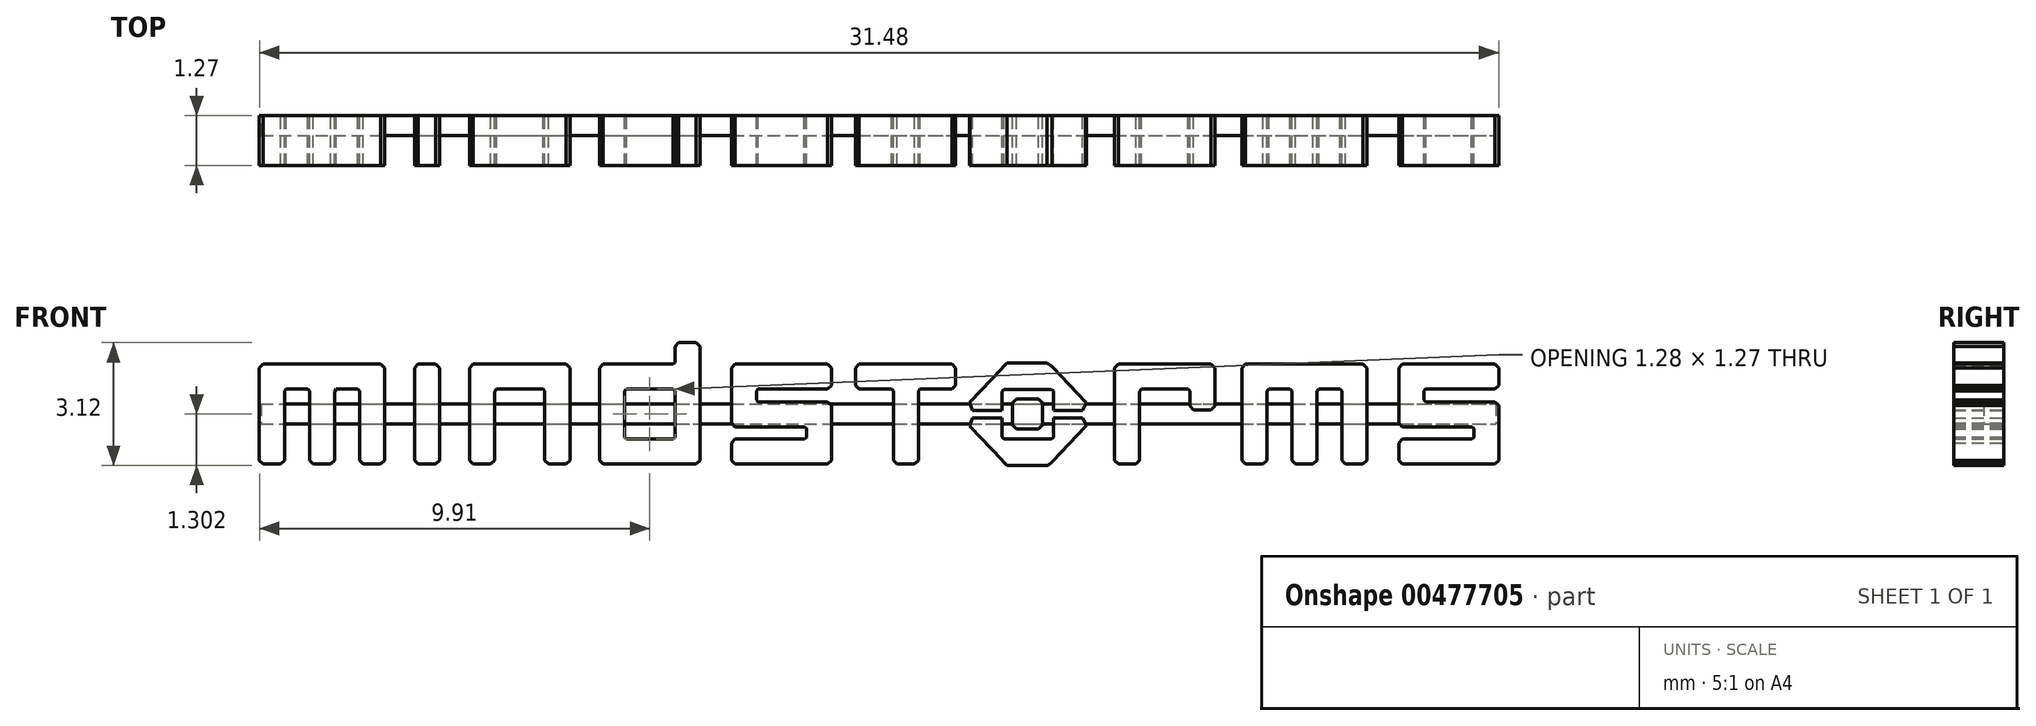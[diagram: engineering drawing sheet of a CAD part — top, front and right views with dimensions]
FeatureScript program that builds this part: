
annotation { "Feature Type Name" : "Feature", "Feature Type Description" : "" }
export const myFeature = defineFeature(function(context is Context, id is Id, definition is map)
    precondition{}
    {
        {
            var Q0;
            Q0=qCreatedBy(makeId("Front.planeOp"),FACE);
            var sketch = newSketch(context, id + "F0", { "sketchPlane" : qUnion([Q0])});
            skLineSegment(sketch, "E0", {"start": v(4.43, -0.35) * mm, "end": v(5.14, -0.35) * mm});
            skLineSegment(sketch, "E1", {"start": v(5.14, -0.35) * mm, "end": v(5.17, -0.35) * mm});
            skLineSegment(sketch, "E2", {"start": v(5.17, -0.35) * mm, "end": v(5.26, -0.55) * mm});
            skLineSegment(sketch, "E3", {"start": v(5.26, -0.55) * mm, "end": v(5.25, -0.57) * mm});
            skLineSegment(sketch, "E4", {"start": v(5.25, -0.57) * mm, "end": v(4.42, -1.44) * mm});
            skLineSegment(sketch, "E5", {"start": v(4.42, -1.44) * mm, "end": v(4.38, -1.47) * mm});
            skLineSegment(sketch, "E6", {"start": v(4.38, -1.47) * mm, "end": v(4.29, -1.56) * mm});
            skLineSegment(sketch, "E7", {"start": v(4.29, -1.56) * mm, "end": v(4.25, -1.56) * mm});
            skLineSegment(sketch, "E8", {"start": v(4.25, -1.56) * mm, "end": v(3.3, -1.56) * mm});
            skLineSegment(sketch, "E9", {"start": v(3.3, -1.56) * mm, "end": v(3.25, -1.56) * mm});
            skLineSegment(sketch, "E10", {"start": v(3.25, -1.56) * mm, "end": v(3.15, -1.46) * mm});
            skLineSegment(sketch, "E11", {"start": v(3.15, -1.46) * mm, "end": v(3.11, -1.42) * mm});
            skLineSegment(sketch, "E12", {"start": v(3.11, -1.42) * mm, "end": v(2.3, -0.57) * mm});
            skLineSegment(sketch, "E13", {"start": v(2.3, -0.57) * mm, "end": v(2.3, -0.55) * mm});
            skLineSegment(sketch, "E14", {"start": v(2.3, -0.55) * mm, "end": v(2.38, -0.35) * mm});
            skLineSegment(sketch, "E15", {"start": v(2.38, -0.35) * mm, "end": v(2.4, -0.35) * mm});
            skLineSegment(sketch, "E16", {"start": v(2.4, -0.35) * mm, "end": v(3.12, -0.35) * mm});
            skLineSegment(sketch, "E17", {"start": v(3.12, -0.35) * mm, "end": v(3.12, -0.83) * mm});
            skLineSegment(sketch, "E18", {"start": v(3.12, -0.83) * mm, "end": v(3.12, -0.84) * mm});
            skLineSegment(sketch, "E19", {"start": v(3.12, -0.84) * mm, "end": v(3.17, -0.9) * mm});
            skLineSegment(sketch, "E20", {"start": v(3.17, -0.9) * mm, "end": v(3.18, -0.9) * mm});
            skLineSegment(sketch, "E21", {"start": v(3.18, -0.9) * mm, "end": v(4.36, -0.9) * mm});
            skLineSegment(sketch, "E22", {"start": v(4.36, -0.9) * mm, "end": v(4.38, -0.9) * mm});
            skLineSegment(sketch, "E23", {"start": v(4.38, -0.9) * mm, "end": v(4.43, -0.84) * mm});
            skLineSegment(sketch, "E24", {"start": v(4.43, -0.84) * mm, "end": v(4.43, -0.83) * mm});
            skLineSegment(sketch, "E25", {"start": v(4.43, -0.83) * mm, "end": v(4.43, -0.35) * mm});
            skLineSegment(sketch, "E26", {"start": v(4.43, -0.16) * mm, "end": v(5.14, -0.16) * mm});
            skLineSegment(sketch, "E27", {"start": v(5.14, -0.16) * mm, "end": v(5.17, -0.16) * mm});
            skLineSegment(sketch, "E28", {"start": v(5.17, -0.16) * mm, "end": v(5.26, 0.04) * mm});
            skLineSegment(sketch, "E29", {"start": v(5.26, 0.04) * mm, "end": v(5.25, 0.05) * mm});
            skLineSegment(sketch, "E30", {"start": v(5.25, 0.05) * mm, "end": v(4.42, 0.93) * mm});
            skLineSegment(sketch, "E31", {"start": v(4.42, 0.93) * mm, "end": v(4.39, 0.96) * mm});
            skLineSegment(sketch, "E32", {"start": v(4.39, 0.96) * mm, "end": v(4.26, 1.05) * mm});
            skLineSegment(sketch, "E33", {"start": v(4.26, 1.05) * mm, "end": v(4.25, 1.05) * mm});
            skLineSegment(sketch, "E34", {"start": v(4.25, 1.05) * mm, "end": v(3.3, 1.05) * mm});
            skLineSegment(sketch, "E35", {"start": v(3.3, 1.05) * mm, "end": v(3.25, 1.05) * mm});
            skLineSegment(sketch, "E36", {"start": v(3.25, 1.05) * mm, "end": v(3.15, 0.94) * mm});
            skLineSegment(sketch, "E37", {"start": v(3.15, 0.94) * mm, "end": v(3.11, 0.9) * mm});
            skLineSegment(sketch, "E38", {"start": v(3.11, 0.9) * mm, "end": v(2.3, 0.05) * mm});
            skLineSegment(sketch, "E39", {"start": v(2.3, 0.05) * mm, "end": v(2.3, 0.04) * mm});
            skLineSegment(sketch, "E40", {"start": v(2.3, 0.04) * mm, "end": v(2.38, -0.16) * mm});
            skLineSegment(sketch, "E41", {"start": v(2.38, -0.16) * mm, "end": v(2.4, -0.16) * mm});
            skLineSegment(sketch, "E42", {"start": v(2.4, -0.16) * mm, "end": v(3.12, -0.16) * mm});
            skLineSegment(sketch, "E43", {"start": v(3.12, -0.16) * mm, "end": v(3.12, 0.31) * mm});
            skLineSegment(sketch, "E44", {"start": v(3.12, 0.31) * mm, "end": v(3.12, 0.32) * mm});
            skLineSegment(sketch, "E45", {"start": v(3.12, 0.32) * mm, "end": v(3.17, 0.38) * mm});
            skLineSegment(sketch, "E46", {"start": v(3.17, 0.38) * mm, "end": v(3.19, 0.38) * mm});
            skLineSegment(sketch, "E47", {"start": v(3.19, 0.38) * mm, "end": v(4.36, 0.38) * mm});
            skLineSegment(sketch, "E48", {"start": v(4.36, 0.38) * mm, "end": v(4.38, 0.38) * mm});
            skLineSegment(sketch, "E49", {"start": v(4.38, 0.38) * mm, "end": v(4.43, 0.33) * mm});
            skLineSegment(sketch, "E50", {"start": v(4.43, 0.33) * mm, "end": v(4.43, 0.31) * mm});
            skLineSegment(sketch, "E51", {"start": v(4.43, 0.31) * mm, "end": v(4.43, -0.16) * mm});
            skLineSegment(sketch, "E52", {"start": v(8.4, 1.01) * mm, "end": v(6.1, 1.01) * mm});
            skLineSegment(sketch, "E53", {"start": v(6.1, 1.01) * mm, "end": v(6.08, 1.01) * mm});
            skLineSegment(sketch, "E54", {"start": v(6.08, 1.01) * mm, "end": v(5.98, 0.92) * mm});
            skLineSegment(sketch, "E55", {"start": v(5.98, 0.92) * mm, "end": v(5.98, 0.89) * mm});
            skLineSegment(sketch, "E56", {"start": v(5.98, 0.89) * mm, "end": v(5.98, -1.4) * mm});
            skLineSegment(sketch, "E57", {"start": v(5.98, -1.4) * mm, "end": v(5.98, -1.43) * mm});
            skLineSegment(sketch, "E58", {"start": v(5.98, -1.43) * mm, "end": v(6.08, -1.53) * mm});
            skLineSegment(sketch, "E59", {"start": v(6.08, -1.53) * mm, "end": v(6.1, -1.53) * mm});
            skLineSegment(sketch, "E60", {"start": v(6.1, -1.53) * mm, "end": v(6.49, -1.53) * mm});
            skLineSegment(sketch, "E61", {"start": v(6.49, -1.53) * mm, "end": v(6.52, -1.53) * mm});
            skLineSegment(sketch, "E62", {"start": v(6.52, -1.53) * mm, "end": v(6.62, -1.43) * mm});
            skLineSegment(sketch, "E63", {"start": v(6.62, -1.43) * mm, "end": v(6.62, -1.4) * mm});
            skLineSegment(sketch, "E64", {"start": v(6.62, -1.4) * mm, "end": v(6.62, 0.32) * mm});
            skLineSegment(sketch, "E65", {"start": v(6.62, 0.32) * mm, "end": v(6.62, 0.32) * mm});
            skLineSegment(sketch, "E66", {"start": v(6.62, 0.32) * mm, "end": v(6.66, 0.38) * mm});
            skLineSegment(sketch, "E67", {"start": v(6.66, 0.38) * mm, "end": v(6.68, 0.38) * mm});
            skLineSegment(sketch, "E68", {"start": v(6.68, 0.38) * mm, "end": v(7.83, 0.38) * mm});
            skLineSegment(sketch, "E69", {"start": v(7.83, 0.38) * mm, "end": v(7.84, 0.38) * mm});
            skLineSegment(sketch, "E70", {"start": v(7.84, 0.38) * mm, "end": v(7.9, 0.33) * mm});
            skLineSegment(sketch, "E71", {"start": v(7.9, 0.33) * mm, "end": v(7.9, 0.32) * mm});
            skLineSegment(sketch, "E72", {"start": v(7.9, 0.32) * mm, "end": v(7.9, -0.02) * mm});
            skLineSegment(sketch, "E73", {"start": v(7.9, -0.02) * mm, "end": v(7.9, -0.05) * mm});
            skLineSegment(sketch, "E74", {"start": v(7.9, -0.05) * mm, "end": v(7.99, -0.15) * mm});
            skLineSegment(sketch, "E75", {"start": v(7.99, -0.15) * mm, "end": v(8.02, -0.15) * mm});
            skLineSegment(sketch, "E76", {"start": v(8.02, -0.15) * mm, "end": v(8.4, -0.15) * mm});
            skLineSegment(sketch, "E77", {"start": v(8.4, -0.15) * mm, "end": v(8.43, -0.15) * mm});
            skLineSegment(sketch, "E78", {"start": v(8.43, -0.15) * mm, "end": v(8.53, -0.05) * mm});
            skLineSegment(sketch, "E79", {"start": v(8.53, -0.05) * mm, "end": v(8.53, -0.02) * mm});
            skLineSegment(sketch, "E80", {"start": v(8.53, -0.02) * mm, "end": v(8.53, 0.89) * mm});
            skLineSegment(sketch, "E81", {"start": v(8.53, 0.89) * mm, "end": v(8.53, 0.92) * mm});
            skLineSegment(sketch, "E82", {"start": v(8.53, 0.92) * mm, "end": v(8.43, 1.01) * mm});
            skLineSegment(sketch, "E83", {"start": v(8.43, 1.01) * mm, "end": v(8.4, 1.01) * mm});
            skLineSegment(sketch, "E84", {"start": v(13.84, 0.32) * mm, "end": v(13.84, 0.33) * mm});
            skLineSegment(sketch, "E85", {"start": v(13.84, 0.33) * mm, "end": v(13.88, 0.38) * mm});
            skLineSegment(sketch, "E86", {"start": v(13.88, 0.38) * mm, "end": v(13.9, 0.38) * mm});
            skLineSegment(sketch, "E87", {"start": v(13.9, 0.38) * mm, "end": v(15.62, 0.38) * mm});
            skLineSegment(sketch, "E88", {"start": v(15.62, 0.38) * mm, "end": v(15.65, 0.38) * mm});
            skLineSegment(sketch, "E89", {"start": v(15.65, 0.38) * mm, "end": v(15.74, 0.47) * mm});
            skLineSegment(sketch, "E90", {"start": v(15.74, 0.47) * mm, "end": v(15.74, 0.5) * mm});
            skLineSegment(sketch, "E91", {"start": v(15.74, 0.5) * mm, "end": v(15.74, 0.89) * mm});
            skLineSegment(sketch, "E92", {"start": v(15.74, 0.89) * mm, "end": v(15.74, 0.92) * mm});
            skLineSegment(sketch, "E93", {"start": v(15.74, 0.92) * mm, "end": v(15.65, 1.01) * mm});
            skLineSegment(sketch, "E94", {"start": v(15.65, 1.01) * mm, "end": v(15.62, 1.01) * mm});
            skLineSegment(sketch, "E95", {"start": v(15.62, 1.01) * mm, "end": v(13.33, 1.01) * mm});
            skLineSegment(sketch, "E96", {"start": v(13.33, 1.01) * mm, "end": v(13.3, 1.01) * mm});
            skLineSegment(sketch, "E97", {"start": v(13.3, 1.01) * mm, "end": v(13.2, 0.92) * mm});
            skLineSegment(sketch, "E98", {"start": v(13.2, 0.92) * mm, "end": v(13.2, 0.89) * mm});
            skLineSegment(sketch, "E99", {"start": v(13.2, 0.89) * mm, "end": v(13.2, -0.45) * mm});
            skLineSegment(sketch, "E100", {"start": v(13.2, -0.45) * mm, "end": v(13.2, -0.48) * mm});
            skLineSegment(sketch, "E101", {"start": v(13.2, -0.48) * mm, "end": v(13.3, -0.58) * mm});
            skLineSegment(sketch, "E102", {"start": v(13.3, -0.58) * mm, "end": v(13.33, -0.58) * mm});
            skLineSegment(sketch, "E103", {"start": v(13.33, -0.58) * mm, "end": v(15.05, -0.58) * mm});
            skLineSegment(sketch, "E104", {"start": v(15.05, -0.58) * mm, "end": v(15.06, -0.58) * mm});
            skLineSegment(sketch, "E105", {"start": v(15.06, -0.58) * mm, "end": v(15.1, -0.62) * mm});
            skLineSegment(sketch, "E106", {"start": v(15.1, -0.62) * mm, "end": v(15.1, -0.64) * mm});
            skLineSegment(sketch, "E107", {"start": v(15.1, -0.64) * mm, "end": v(15.1, -0.83) * mm});
            skLineSegment(sketch, "E108", {"start": v(15.1, -0.83) * mm, "end": v(15.1, -0.85) * mm});
            skLineSegment(sketch, "E109", {"start": v(15.1, -0.85) * mm, "end": v(15.06, -0.9) * mm});
            skLineSegment(sketch, "E110", {"start": v(15.06, -0.9) * mm, "end": v(15.05, -0.9) * mm});
            skLineSegment(sketch, "E111", {"start": v(15.05, -0.9) * mm, "end": v(13.33, -0.9) * mm});
            skLineSegment(sketch, "E112", {"start": v(13.33, -0.9) * mm, "end": v(13.3, -0.9) * mm});
            skLineSegment(sketch, "E113", {"start": v(13.3, -0.9) * mm, "end": v(13.2, -1) * mm});
            skLineSegment(sketch, "E114", {"start": v(13.2, -1) * mm, "end": v(13.2, -1.02) * mm});
            skLineSegment(sketch, "E115", {"start": v(13.2, -1.02) * mm, "end": v(13.2, -1.4) * mm});
            skLineSegment(sketch, "E116", {"start": v(13.2, -1.4) * mm, "end": v(13.2, -1.43) * mm});
            skLineSegment(sketch, "E117", {"start": v(13.2, -1.43) * mm, "end": v(13.3, -1.53) * mm});
            skLineSegment(sketch, "E118", {"start": v(13.3, -1.53) * mm, "end": v(13.33, -1.53) * mm});
            skLineSegment(sketch, "E119", {"start": v(13.33, -1.53) * mm, "end": v(15.62, -1.53) * mm});
            skLineSegment(sketch, "E120", {"start": v(15.62, -1.53) * mm, "end": v(15.65, -1.53) * mm});
            skLineSegment(sketch, "E121", {"start": v(15.65, -1.53) * mm, "end": v(15.74, -1.43) * mm});
            skLineSegment(sketch, "E122", {"start": v(15.74, -1.43) * mm, "end": v(15.74, -1.4) * mm});
            skLineSegment(sketch, "E123", {"start": v(15.74, -1.4) * mm, "end": v(15.74, -0.07) * mm});
            skLineSegment(sketch, "E124", {"start": v(15.74, -0.07) * mm, "end": v(15.74, -0.04) * mm});
            skLineSegment(sketch, "E125", {"start": v(15.74, -0.04) * mm, "end": v(15.65, 0.06) * mm});
            skLineSegment(sketch, "E126", {"start": v(15.65, 0.06) * mm, "end": v(15.62, 0.06) * mm});
            skLineSegment(sketch, "E127", {"start": v(15.62, 0.06) * mm, "end": v(13.9, 0.06) * mm});
            skLineSegment(sketch, "E128", {"start": v(13.9, 0.06) * mm, "end": v(13.88, 0.06) * mm});
            skLineSegment(sketch, "E129", {"start": v(13.88, 0.06) * mm, "end": v(13.84, 0.1) * mm});
            skLineSegment(sketch, "E130", {"start": v(13.84, 0.1) * mm, "end": v(13.84, 0.12) * mm});
            skLineSegment(sketch, "E131", {"start": v(13.84, 0.12) * mm, "end": v(13.84, 0.32) * mm});
            skLineSegment(sketch, "E132", {"start": v(-3.12, 0.32) * mm, "end": v(-3.12, 0.33) * mm});
            skLineSegment(sketch, "E133", {"start": v(-3.12, 0.33) * mm, "end": v(-3.08, 0.38) * mm});
            skLineSegment(sketch, "E134", {"start": v(-3.08, 0.38) * mm, "end": v(-3.06, 0.38) * mm});
            skLineSegment(sketch, "E135", {"start": v(-3.06, 0.38) * mm, "end": v(-1.34, 0.38) * mm});
            skLineSegment(sketch, "E136", {"start": v(-1.34, 0.38) * mm, "end": v(-1.31, 0.38) * mm});
            skLineSegment(sketch, "E137", {"start": v(-1.31, 0.38) * mm, "end": v(-1.21, 0.47) * mm});
            skLineSegment(sketch, "E138", {"start": v(-1.21, 0.47) * mm, "end": v(-1.21, 0.5) * mm});
            skLineSegment(sketch, "E139", {"start": v(-1.21, 0.5) * mm, "end": v(-1.21, 0.89) * mm});
            skLineSegment(sketch, "E140", {"start": v(-1.21, 0.89) * mm, "end": v(-1.21, 0.92) * mm});
            skLineSegment(sketch, "E141", {"start": v(-1.21, 0.92) * mm, "end": v(-1.31, 1.01) * mm});
            skLineSegment(sketch, "E142", {"start": v(-1.31, 1.01) * mm, "end": v(-1.34, 1.01) * mm});
            skLineSegment(sketch, "E143", {"start": v(-1.34, 1.01) * mm, "end": v(-3.63, 1.01) * mm});
            skLineSegment(sketch, "E144", {"start": v(-3.63, 1.01) * mm, "end": v(-3.66, 1.01) * mm});
            skLineSegment(sketch, "E145", {"start": v(-3.66, 1.01) * mm, "end": v(-3.76, 0.92) * mm});
            skLineSegment(sketch, "E146", {"start": v(-3.76, 0.92) * mm, "end": v(-3.76, 0.89) * mm});
            skLineSegment(sketch, "E147", {"start": v(-3.76, 0.89) * mm, "end": v(-3.76, -0.45) * mm});
            skLineSegment(sketch, "E148", {"start": v(-3.76, -0.45) * mm, "end": v(-3.76, -0.48) * mm});
            skLineSegment(sketch, "E149", {"start": v(-3.76, -0.48) * mm, "end": v(-3.66, -0.58) * mm});
            skLineSegment(sketch, "E150", {"start": v(-3.66, -0.58) * mm, "end": v(-3.63, -0.58) * mm});
            skLineSegment(sketch, "E151", {"start": v(-3.63, -0.58) * mm, "end": v(-1.9, -0.58) * mm});
            skLineSegment(sketch, "E152", {"start": v(-1.9, -0.58) * mm, "end": v(-1.9, -0.58) * mm});
            skLineSegment(sketch, "E153", {"start": v(-1.9, -0.58) * mm, "end": v(-1.85, -0.62) * mm});
            skLineSegment(sketch, "E154", {"start": v(-1.85, -0.62) * mm, "end": v(-1.85, -0.64) * mm});
            skLineSegment(sketch, "E155", {"start": v(-1.85, -0.64) * mm, "end": v(-1.85, -0.83) * mm});
            skLineSegment(sketch, "E156", {"start": v(-1.85, -0.83) * mm, "end": v(-1.85, -0.85) * mm});
            skLineSegment(sketch, "E157", {"start": v(-1.85, -0.85) * mm, "end": v(-1.9, -0.9) * mm});
            skLineSegment(sketch, "E158", {"start": v(-1.9, -0.9) * mm, "end": v(-1.9, -0.9) * mm});
            skLineSegment(sketch, "E159", {"start": v(-1.9, -0.9) * mm, "end": v(-3.63, -0.9) * mm});
            skLineSegment(sketch, "E160", {"start": v(-3.63, -0.9) * mm, "end": v(-3.66, -0.9) * mm});
            skLineSegment(sketch, "E161", {"start": v(-3.66, -0.9) * mm, "end": v(-3.76, -1) * mm});
            skLineSegment(sketch, "E162", {"start": v(-3.76, -1) * mm, "end": v(-3.76, -1.02) * mm});
            skLineSegment(sketch, "E163", {"start": v(-3.76, -1.02) * mm, "end": v(-3.76, -1.4) * mm});
            skLineSegment(sketch, "E164", {"start": v(-3.76, -1.4) * mm, "end": v(-3.76, -1.43) * mm});
            skLineSegment(sketch, "E165", {"start": v(-3.76, -1.43) * mm, "end": v(-3.66, -1.53) * mm});
            skLineSegment(sketch, "E166", {"start": v(-3.66, -1.53) * mm, "end": v(-3.63, -1.53) * mm});
            skLineSegment(sketch, "E167", {"start": v(-3.63, -1.53) * mm, "end": v(-1.34, -1.53) * mm});
            skLineSegment(sketch, "E168", {"start": v(-1.34, -1.53) * mm, "end": v(-1.31, -1.53) * mm});
            skLineSegment(sketch, "E169", {"start": v(-1.31, -1.53) * mm, "end": v(-1.21, -1.43) * mm});
            skLineSegment(sketch, "E170", {"start": v(-1.21, -1.43) * mm, "end": v(-1.21, -1.4) * mm});
            skLineSegment(sketch, "E171", {"start": v(-1.21, -1.4) * mm, "end": v(-1.21, -0.07) * mm});
            skLineSegment(sketch, "E172", {"start": v(-1.21, -0.07) * mm, "end": v(-1.21, -0.04) * mm});
            skLineSegment(sketch, "E173", {"start": v(-1.21, -0.04) * mm, "end": v(-1.31, 0.06) * mm});
            skLineSegment(sketch, "E174", {"start": v(-1.31, 0.06) * mm, "end": v(-1.34, 0.06) * mm});
            skLineSegment(sketch, "E175", {"start": v(-1.34, 0.06) * mm, "end": v(-3.06, 0.06) * mm});
            skLineSegment(sketch, "E176", {"start": v(-3.06, 0.06) * mm, "end": v(-3.07, 0.06) * mm});
            skLineSegment(sketch, "E177", {"start": v(-3.07, 0.06) * mm, "end": v(-3.12, 0.1) * mm});
            skLineSegment(sketch, "E178", {"start": v(-3.12, 0.1) * mm, "end": v(-3.12, 0.12) * mm});
            skLineSegment(sketch, "E179", {"start": v(-3.12, 0.12) * mm, "end": v(-3.12, 0.32) * mm});
            skLineSegment(sketch, "E180", {"start": v(-5.2, -0.83) * mm, "end": v(-5.2, -0.85) * mm});
            skLineSegment(sketch, "E181", {"start": v(-5.2, -0.85) * mm, "end": v(-5.24, -0.9) * mm});
            skLineSegment(sketch, "E182", {"start": v(-5.24, -0.9) * mm, "end": v(-5.25, -0.9) * mm});
            skLineSegment(sketch, "E183", {"start": v(-5.25, -0.9) * mm, "end": v(-6.4, -0.9) * mm});
            skLineSegment(sketch, "E184", {"start": v(-6.4, -0.9) * mm, "end": v(-6.42, -0.9) * mm});
            skLineSegment(sketch, "E185", {"start": v(-6.42, -0.9) * mm, "end": v(-6.47, -0.85) * mm});
            skLineSegment(sketch, "E186", {"start": v(-6.47, -0.85) * mm, "end": v(-6.47, -0.83) * mm});
            skLineSegment(sketch, "E187", {"start": v(-6.47, -0.83) * mm, "end": v(-6.47, 0.32) * mm});
            skLineSegment(sketch, "E188", {"start": v(-6.47, 0.32) * mm, "end": v(-6.47, 0.33) * mm});
            skLineSegment(sketch, "E189", {"start": v(-6.47, 0.33) * mm, "end": v(-6.42, 0.38) * mm});
            skLineSegment(sketch, "E190", {"start": v(-6.42, 0.38) * mm, "end": v(-6.4, 0.38) * mm});
            skLineSegment(sketch, "E191", {"start": v(-6.4, 0.38) * mm, "end": v(-5.25, 0.38) * mm});
            skLineSegment(sketch, "E192", {"start": v(-5.25, 0.38) * mm, "end": v(-5.24, 0.38) * mm});
            skLineSegment(sketch, "E193", {"start": v(-5.24, 0.38) * mm, "end": v(-5.2, 0.33) * mm});
            skLineSegment(sketch, "E194", {"start": v(-5.2, 0.33) * mm, "end": v(-5.2, 0.32) * mm});
            skLineSegment(sketch, "E195", {"start": v(-5.2, 0.32) * mm, "end": v(-5.2, -0.83) * mm});
            skLineSegment(sketch, "E196", {"start": v(-4.68, 1.56) * mm, "end": v(-5.06, 1.56) * mm});
            skLineSegment(sketch, "E197", {"start": v(-5.06, 1.56) * mm, "end": v(-5.1, 1.56) * mm});
            skLineSegment(sketch, "E198", {"start": v(-5.1, 1.56) * mm, "end": v(-5.2, 1.47) * mm});
            skLineSegment(sketch, "E199", {"start": v(-5.2, 1.47) * mm, "end": v(-5.2, 1.43) * mm});
            skLineSegment(sketch, "E200", {"start": v(-5.2, 1.43) * mm, "end": v(-5.2, 1.08) * mm});
            skLineSegment(sketch, "E201", {"start": v(-5.2, 1.08) * mm, "end": v(-5.2, 1.06) * mm});
            skLineSegment(sketch, "E202", {"start": v(-5.2, 1.06) * mm, "end": v(-5.24, 1.01) * mm});
            skLineSegment(sketch, "E203", {"start": v(-5.24, 1.01) * mm, "end": v(-5.25, 1.01) * mm});
            skLineSegment(sketch, "E204", {"start": v(-5.25, 1.01) * mm, "end": v(-6.98, 1.01) * mm});
            skLineSegment(sketch, "E205", {"start": v(-6.98, 1.01) * mm, "end": v(-7.01, 1.01) * mm});
            skLineSegment(sketch, "E206", {"start": v(-7.01, 1.01) * mm, "end": v(-7.1, 0.92) * mm});
            skLineSegment(sketch, "E207", {"start": v(-7.1, 0.92) * mm, "end": v(-7.1, 0.89) * mm});
            skLineSegment(sketch, "E208", {"start": v(-7.1, 0.89) * mm, "end": v(-7.1, -1.4) * mm});
            skLineSegment(sketch, "E209", {"start": v(-7.1, -1.4) * mm, "end": v(-7.1, -1.43) * mm});
            skLineSegment(sketch, "E210", {"start": v(-7.1, -1.43) * mm, "end": v(-7.01, -1.53) * mm});
            skLineSegment(sketch, "E211", {"start": v(-7.01, -1.53) * mm, "end": v(-6.98, -1.53) * mm});
            skLineSegment(sketch, "E212", {"start": v(-6.98, -1.53) * mm, "end": v(-4.68, -1.53) * mm});
            skLineSegment(sketch, "E213", {"start": v(-4.68, -1.53) * mm, "end": v(-4.65, -1.53) * mm});
            skLineSegment(sketch, "E214", {"start": v(-4.65, -1.53) * mm, "end": v(-4.56, -1.43) * mm});
            skLineSegment(sketch, "E215", {"start": v(-4.56, -1.43) * mm, "end": v(-4.56, -1.4) * mm});
            skLineSegment(sketch, "E216", {"start": v(-4.56, -1.4) * mm, "end": v(-4.56, 1.43) * mm});
            skLineSegment(sketch, "E217", {"start": v(-4.56, 1.43) * mm, "end": v(-4.56, 1.47) * mm});
            skLineSegment(sketch, "E218", {"start": v(-4.56, 1.47) * mm, "end": v(-4.65, 1.56) * mm});
            skLineSegment(sketch, "E219", {"start": v(-4.65, 1.56) * mm, "end": v(-4.68, 1.56) * mm});
            skLineSegment(sketch, "E220", {"start": v(1.81, 1.01) * mm, "end": v(-0.47, 1.01) * mm});
            skLineSegment(sketch, "E221", {"start": v(-0.47, 1.01) * mm, "end": v(-0.5, 1.01) * mm});
            skLineSegment(sketch, "E222", {"start": v(-0.5, 1.01) * mm, "end": v(-0.6, 0.92) * mm});
            skLineSegment(sketch, "E223", {"start": v(-0.6, 0.92) * mm, "end": v(-0.6, 0.89) * mm});
            skLineSegment(sketch, "E224", {"start": v(-0.6, 0.89) * mm, "end": v(-0.6, 0.5) * mm});
            skLineSegment(sketch, "E225", {"start": v(-0.6, 0.5) * mm, "end": v(-0.6, 0.47) * mm});
            skLineSegment(sketch, "E226", {"start": v(-0.6, 0.47) * mm, "end": v(-0.5, 0.38) * mm});
            skLineSegment(sketch, "E227", {"start": v(-0.5, 0.38) * mm, "end": v(-0.47, 0.38) * mm});
            skLineSegment(sketch, "E228", {"start": v(-0.47, 0.38) * mm, "end": v(0.3, 0.38) * mm});
            skLineSegment(sketch, "E229", {"start": v(0.3, 0.38) * mm, "end": v(0.31, 0.38) * mm});
            skLineSegment(sketch, "E230", {"start": v(0.31, 0.38) * mm, "end": v(0.36, 0.33) * mm});
            skLineSegment(sketch, "E231", {"start": v(0.36, 0.33) * mm, "end": v(0.36, 0.32) * mm});
            skLineSegment(sketch, "E232", {"start": v(0.36, 0.32) * mm, "end": v(0.36, -1.4) * mm});
            skLineSegment(sketch, "E233", {"start": v(0.36, -1.4) * mm, "end": v(0.36, -1.43) * mm});
            skLineSegment(sketch, "E234", {"start": v(0.36, -1.43) * mm, "end": v(0.45, -1.53) * mm});
            skLineSegment(sketch, "E235", {"start": v(0.45, -1.53) * mm, "end": v(0.49, -1.53) * mm});
            skLineSegment(sketch, "E236", {"start": v(0.49, -1.53) * mm, "end": v(0.87, -1.53) * mm});
            skLineSegment(sketch, "E237", {"start": v(0.87, -1.53) * mm, "end": v(0.9, -1.53) * mm});
            skLineSegment(sketch, "E238", {"start": v(0.9, -1.53) * mm, "end": v(1, -1.43) * mm});
            skLineSegment(sketch, "E239", {"start": v(1, -1.43) * mm, "end": v(1, -1.4) * mm});
            skLineSegment(sketch, "E240", {"start": v(1, -1.4) * mm, "end": v(1, 0.32) * mm});
            skLineSegment(sketch, "E241", {"start": v(1, 0.32) * mm, "end": v(1, 0.33) * mm});
            skLineSegment(sketch, "E242", {"start": v(1, 0.33) * mm, "end": v(1.04, 0.38) * mm});
            skLineSegment(sketch, "E243", {"start": v(1.04, 0.38) * mm, "end": v(1.06, 0.38) * mm});
            skLineSegment(sketch, "E244", {"start": v(1.06, 0.38) * mm, "end": v(1.81, 0.38) * mm});
            skLineSegment(sketch, "E245", {"start": v(1.81, 0.38) * mm, "end": v(1.84, 0.38) * mm});
            skLineSegment(sketch, "E246", {"start": v(1.84, 0.38) * mm, "end": v(1.94, 0.47) * mm});
            skLineSegment(sketch, "E247", {"start": v(1.94, 0.47) * mm, "end": v(1.94, 0.5) * mm});
            skLineSegment(sketch, "E248", {"start": v(1.94, 0.5) * mm, "end": v(1.94, 0.89) * mm});
            skLineSegment(sketch, "E249", {"start": v(1.94, 0.89) * mm, "end": v(1.94, 0.92) * mm});
            skLineSegment(sketch, "E250", {"start": v(1.94, 0.92) * mm, "end": v(1.84, 1.01) * mm});
            skLineSegment(sketch, "E251", {"start": v(1.84, 1.01) * mm, "end": v(1.81, 1.01) * mm});
            skLineSegment(sketch, "E252", {"start": v(-7.98, 1.01) * mm, "end": v(-10.28, 1.01) * mm});
            skLineSegment(sketch, "E253", {"start": v(-10.28, 1.01) * mm, "end": v(-10.31, 1.01) * mm});
            skLineSegment(sketch, "E254", {"start": v(-10.31, 1.01) * mm, "end": v(-10.4, 0.92) * mm});
            skLineSegment(sketch, "E255", {"start": v(-10.4, 0.92) * mm, "end": v(-10.4, 0.89) * mm});
            skLineSegment(sketch, "E256", {"start": v(-10.4, 0.89) * mm, "end": v(-10.4, -1.4) * mm});
            skLineSegment(sketch, "E257", {"start": v(-10.4, -1.4) * mm, "end": v(-10.4, -1.43) * mm});
            skLineSegment(sketch, "E258", {"start": v(-10.4, -1.43) * mm, "end": v(-10.31, -1.53) * mm});
            skLineSegment(sketch, "E259", {"start": v(-10.31, -1.53) * mm, "end": v(-10.28, -1.53) * mm});
            skLineSegment(sketch, "E260", {"start": v(-10.28, -1.53) * mm, "end": v(-9.9, -1.53) * mm});
            skLineSegment(sketch, "E261", {"start": v(-9.9, -1.53) * mm, "end": v(-9.87, -1.53) * mm});
            skLineSegment(sketch, "E262", {"start": v(-9.87, -1.53) * mm, "end": v(-9.77, -1.43) * mm});
            skLineSegment(sketch, "E263", {"start": v(-9.77, -1.43) * mm, "end": v(-9.77, -1.4) * mm});
            skLineSegment(sketch, "E264", {"start": v(-9.77, -1.4) * mm, "end": v(-9.77, 0.32) * mm});
            skLineSegment(sketch, "E265", {"start": v(-9.77, 0.32) * mm, "end": v(-9.77, 0.32) * mm});
            skLineSegment(sketch, "E266", {"start": v(-9.77, 0.32) * mm, "end": v(-9.72, 0.38) * mm});
            skLineSegment(sketch, "E267", {"start": v(-9.72, 0.38) * mm, "end": v(-9.7, 0.38) * mm});
            skLineSegment(sketch, "E268", {"start": v(-9.7, 0.38) * mm, "end": v(-8.56, 0.38) * mm});
            skLineSegment(sketch, "E269", {"start": v(-8.56, 0.38) * mm, "end": v(-8.54, 0.38) * mm});
            skLineSegment(sketch, "E270", {"start": v(-8.54, 0.38) * mm, "end": v(-8.5, 0.33) * mm});
            skLineSegment(sketch, "E271", {"start": v(-8.5, 0.33) * mm, "end": v(-8.5, 0.32) * mm});
            skLineSegment(sketch, "E272", {"start": v(-8.5, 0.32) * mm, "end": v(-8.5, -1.4) * mm});
            skLineSegment(sketch, "E273", {"start": v(-8.5, -1.4) * mm, "end": v(-8.5, -1.43) * mm});
            skLineSegment(sketch, "E274", {"start": v(-8.5, -1.43) * mm, "end": v(-8.4, -1.53) * mm});
            skLineSegment(sketch, "E275", {"start": v(-8.4, -1.53) * mm, "end": v(-8.37, -1.53) * mm});
            skLineSegment(sketch, "E276", {"start": v(-8.37, -1.53) * mm, "end": v(-7.98, -1.53) * mm});
            skLineSegment(sketch, "E277", {"start": v(-7.98, -1.53) * mm, "end": v(-7.95, -1.53) * mm});
            skLineSegment(sketch, "E278", {"start": v(-7.95, -1.53) * mm, "end": v(-7.86, -1.43) * mm});
            skLineSegment(sketch, "E279", {"start": v(-7.86, -1.43) * mm, "end": v(-7.86, -1.4) * mm});
            skLineSegment(sketch, "E280", {"start": v(-7.86, -1.4) * mm, "end": v(-7.86, 0.89) * mm});
            skLineSegment(sketch, "E281", {"start": v(-7.86, 0.89) * mm, "end": v(-7.86, 0.92) * mm});
            skLineSegment(sketch, "E282", {"start": v(-7.86, 0.92) * mm, "end": v(-7.95, 1.01) * mm});
            skLineSegment(sketch, "E283", {"start": v(-7.95, 1.01) * mm, "end": v(-7.98, 1.01) * mm});
            skLineSegment(sketch, "E284", {"start": v(12.26, 1.01) * mm, "end": v(9.34, 1.01) * mm});
            skLineSegment(sketch, "E285", {"start": v(9.34, 1.01) * mm, "end": v(9.31, 1.01) * mm});
            skLineSegment(sketch, "E286", {"start": v(9.31, 1.01) * mm, "end": v(9.21, 0.92) * mm});
            skLineSegment(sketch, "E287", {"start": v(9.21, 0.92) * mm, "end": v(9.21, 0.89) * mm});
            skLineSegment(sketch, "E288", {"start": v(9.21, 0.89) * mm, "end": v(9.21, -1.4) * mm});
            skLineSegment(sketch, "E289", {"start": v(9.21, -1.4) * mm, "end": v(9.21, -1.43) * mm});
            skLineSegment(sketch, "E290", {"start": v(9.21, -1.43) * mm, "end": v(9.31, -1.53) * mm});
            skLineSegment(sketch, "E291", {"start": v(9.31, -1.53) * mm, "end": v(9.34, -1.53) * mm});
            skLineSegment(sketch, "E292", {"start": v(9.34, -1.53) * mm, "end": v(9.72, -1.53) * mm});
            skLineSegment(sketch, "E293", {"start": v(9.72, -1.53) * mm, "end": v(9.75, -1.53) * mm});
            skLineSegment(sketch, "E294", {"start": v(9.75, -1.53) * mm, "end": v(9.85, -1.43) * mm});
            skLineSegment(sketch, "E295", {"start": v(9.85, -1.43) * mm, "end": v(9.85, -1.4) * mm});
            skLineSegment(sketch, "E296", {"start": v(9.85, -1.4) * mm, "end": v(9.85, 0.32) * mm});
            skLineSegment(sketch, "E297", {"start": v(9.85, 0.32) * mm, "end": v(9.85, 0.33) * mm});
            skLineSegment(sketch, "E298", {"start": v(9.85, 0.33) * mm, "end": v(9.9, 0.38) * mm});
            skLineSegment(sketch, "E299", {"start": v(9.9, 0.38) * mm, "end": v(9.91, 0.38) * mm});
            skLineSegment(sketch, "E300", {"start": v(9.91, 0.38) * mm, "end": v(10.42, 0.38) * mm});
            skLineSegment(sketch, "E301", {"start": v(10.42, 0.38) * mm, "end": v(10.44, 0.38) * mm});
            skLineSegment(sketch, "E302", {"start": v(10.44, 0.38) * mm, "end": v(10.48, 0.33) * mm});
            skLineSegment(sketch, "E303", {"start": v(10.48, 0.33) * mm, "end": v(10.48, 0.32) * mm});
            skLineSegment(sketch, "E304", {"start": v(10.48, 0.32) * mm, "end": v(10.48, -1.4) * mm});
            skLineSegment(sketch, "E305", {"start": v(10.48, -1.4) * mm, "end": v(10.48, -1.43) * mm});
            skLineSegment(sketch, "E306", {"start": v(10.48, -1.43) * mm, "end": v(10.58, -1.53) * mm});
            skLineSegment(sketch, "E307", {"start": v(10.58, -1.53) * mm, "end": v(10.61, -1.53) * mm});
            skLineSegment(sketch, "E308", {"start": v(10.61, -1.53) * mm, "end": v(11, -1.53) * mm});
            skLineSegment(sketch, "E309", {"start": v(11, -1.53) * mm, "end": v(11.02, -1.53) * mm});
            skLineSegment(sketch, "E310", {"start": v(11.02, -1.53) * mm, "end": v(11.12, -1.43) * mm});
            skLineSegment(sketch, "E311", {"start": v(11.12, -1.43) * mm, "end": v(11.12, -1.4) * mm});
            skLineSegment(sketch, "E312", {"start": v(11.12, -1.4) * mm, "end": v(11.12, 0.32) * mm});
            skLineSegment(sketch, "E313", {"start": v(11.12, 0.32) * mm, "end": v(11.12, 0.33) * mm});
            skLineSegment(sketch, "E314", {"start": v(11.12, 0.33) * mm, "end": v(11.17, 0.38) * mm});
            skLineSegment(sketch, "E315", {"start": v(11.17, 0.38) * mm, "end": v(11.18, 0.38) * mm});
            skLineSegment(sketch, "E316", {"start": v(11.18, 0.38) * mm, "end": v(11.7, 0.38) * mm});
            skLineSegment(sketch, "E317", {"start": v(11.7, 0.38) * mm, "end": v(11.7, 0.38) * mm});
            skLineSegment(sketch, "E318", {"start": v(11.7, 0.38) * mm, "end": v(11.76, 0.33) * mm});
            skLineSegment(sketch, "E319", {"start": v(11.76, 0.33) * mm, "end": v(11.76, 0.32) * mm});
            skLineSegment(sketch, "E320", {"start": v(11.76, 0.32) * mm, "end": v(11.76, -1.4) * mm});
            skLineSegment(sketch, "E321", {"start": v(11.76, -1.4) * mm, "end": v(11.76, -1.43) * mm});
            skLineSegment(sketch, "E322", {"start": v(11.76, -1.43) * mm, "end": v(11.85, -1.53) * mm});
            skLineSegment(sketch, "E323", {"start": v(11.85, -1.53) * mm, "end": v(11.88, -1.53) * mm});
            skLineSegment(sketch, "E324", {"start": v(11.88, -1.53) * mm, "end": v(12.26, -1.53) * mm});
            skLineSegment(sketch, "E325", {"start": v(12.26, -1.53) * mm, "end": v(12.3, -1.53) * mm});
            skLineSegment(sketch, "E326", {"start": v(12.3, -1.53) * mm, "end": v(12.4, -1.43) * mm});
            skLineSegment(sketch, "E327", {"start": v(12.4, -1.43) * mm, "end": v(12.4, -1.4) * mm});
            skLineSegment(sketch, "E328", {"start": v(12.4, -1.4) * mm, "end": v(12.4, 0.89) * mm});
            skLineSegment(sketch, "E329", {"start": v(12.4, 0.89) * mm, "end": v(12.4, 0.92) * mm});
            skLineSegment(sketch, "E330", {"start": v(12.4, 0.92) * mm, "end": v(12.3, 1.01) * mm});
            skLineSegment(sketch, "E331", {"start": v(12.3, 1.01) * mm, "end": v(12.26, 1.01) * mm});
            skLineSegment(sketch, "E332", {"start": v(-12.7, 1.01) * mm, "end": v(-15.62, 1.01) * mm});
            skLineSegment(sketch, "E333", {"start": v(-15.62, 1.01) * mm, "end": v(-15.65, 1.01) * mm});
            skLineSegment(sketch, "E334", {"start": v(-15.65, 1.01) * mm, "end": v(-15.74, 0.92) * mm});
            skLineSegment(sketch, "E335", {"start": v(-15.74, 0.92) * mm, "end": v(-15.74, 0.89) * mm});
            skLineSegment(sketch, "E336", {"start": v(-15.74, 0.89) * mm, "end": v(-15.74, -1.4) * mm});
            skLineSegment(sketch, "E337", {"start": v(-15.74, -1.4) * mm, "end": v(-15.74, -1.43) * mm});
            skLineSegment(sketch, "E338", {"start": v(-15.74, -1.43) * mm, "end": v(-15.65, -1.53) * mm});
            skLineSegment(sketch, "E339", {"start": v(-15.65, -1.53) * mm, "end": v(-15.62, -1.53) * mm});
            skLineSegment(sketch, "E340", {"start": v(-15.62, -1.53) * mm, "end": v(-15.24, -1.53) * mm});
            skLineSegment(sketch, "E341", {"start": v(-15.24, -1.53) * mm, "end": v(-15.2, -1.53) * mm});
            skLineSegment(sketch, "E342", {"start": v(-15.2, -1.53) * mm, "end": v(-15.1, -1.43) * mm});
            skLineSegment(sketch, "E343", {"start": v(-15.1, -1.43) * mm, "end": v(-15.1, -1.4) * mm});
            skLineSegment(sketch, "E344", {"start": v(-15.1, -1.4) * mm, "end": v(-15.1, 0.32) * mm});
            skLineSegment(sketch, "E345", {"start": v(-15.1, 0.32) * mm, "end": v(-15.1, 0.33) * mm});
            skLineSegment(sketch, "E346", {"start": v(-15.1, 0.33) * mm, "end": v(-15.06, 0.38) * mm});
            skLineSegment(sketch, "E347", {"start": v(-15.06, 0.38) * mm, "end": v(-15.04, 0.38) * mm});
            skLineSegment(sketch, "E348", {"start": v(-15.04, 0.38) * mm, "end": v(-14.54, 0.38) * mm});
            skLineSegment(sketch, "E349", {"start": v(-14.54, 0.38) * mm, "end": v(-14.52, 0.38) * mm});
            skLineSegment(sketch, "E350", {"start": v(-14.52, 0.38) * mm, "end": v(-14.47, 0.33) * mm});
            skLineSegment(sketch, "E351", {"start": v(-14.47, 0.33) * mm, "end": v(-14.47, 0.32) * mm});
            skLineSegment(sketch, "E352", {"start": v(-14.47, 0.32) * mm, "end": v(-14.47, -1.4) * mm});
            skLineSegment(sketch, "E353", {"start": v(-14.47, -1.4) * mm, "end": v(-14.47, -1.43) * mm});
            skLineSegment(sketch, "E354", {"start": v(-14.47, -1.43) * mm, "end": v(-14.38, -1.53) * mm});
            skLineSegment(sketch, "E355", {"start": v(-14.38, -1.53) * mm, "end": v(-14.35, -1.53) * mm});
            skLineSegment(sketch, "E356", {"start": v(-14.35, -1.53) * mm, "end": v(-13.96, -1.53) * mm});
            skLineSegment(sketch, "E357", {"start": v(-13.96, -1.53) * mm, "end": v(-13.93, -1.53) * mm});
            skLineSegment(sketch, "E358", {"start": v(-13.93, -1.53) * mm, "end": v(-13.84, -1.43) * mm});
            skLineSegment(sketch, "E359", {"start": v(-13.84, -1.43) * mm, "end": v(-13.84, -1.4) * mm});
            skLineSegment(sketch, "E360", {"start": v(-13.84, -1.4) * mm, "end": v(-13.84, 0.32) * mm});
            skLineSegment(sketch, "E361", {"start": v(-13.84, 0.32) * mm, "end": v(-13.84, 0.32) * mm});
            skLineSegment(sketch, "E362", {"start": v(-13.84, 0.32) * mm, "end": v(-13.8, 0.38) * mm});
            skLineSegment(sketch, "E363", {"start": v(-13.8, 0.38) * mm, "end": v(-13.77, 0.38) * mm});
            skLineSegment(sketch, "E364", {"start": v(-13.77, 0.38) * mm, "end": v(-13.27, 0.38) * mm});
            skLineSegment(sketch, "E365", {"start": v(-13.27, 0.38) * mm, "end": v(-13.25, 0.38) * mm});
            skLineSegment(sketch, "E366", {"start": v(-13.25, 0.38) * mm, "end": v(-13.2, 0.33) * mm});
            skLineSegment(sketch, "E367", {"start": v(-13.2, 0.33) * mm, "end": v(-13.2, 0.32) * mm});
            skLineSegment(sketch, "E368", {"start": v(-13.2, 0.32) * mm, "end": v(-13.2, -1.4) * mm});
            skLineSegment(sketch, "E369", {"start": v(-13.2, -1.4) * mm, "end": v(-13.2, -1.43) * mm});
            skLineSegment(sketch, "E370", {"start": v(-13.2, -1.43) * mm, "end": v(-13.1, -1.53) * mm});
            skLineSegment(sketch, "E371", {"start": v(-13.1, -1.53) * mm, "end": v(-13.08, -1.53) * mm});
            skLineSegment(sketch, "E372", {"start": v(-13.08, -1.53) * mm, "end": v(-12.7, -1.53) * mm});
            skLineSegment(sketch, "E373", {"start": v(-12.7, -1.53) * mm, "end": v(-12.66, -1.53) * mm});
            skLineSegment(sketch, "E374", {"start": v(-12.66, -1.53) * mm, "end": v(-12.57, -1.43) * mm});
            skLineSegment(sketch, "E375", {"start": v(-12.57, -1.43) * mm, "end": v(-12.57, -1.4) * mm});
            skLineSegment(sketch, "E376", {"start": v(-12.57, -1.4) * mm, "end": v(-12.57, 0.89) * mm});
            skLineSegment(sketch, "E377", {"start": v(-12.57, 0.89) * mm, "end": v(-12.57, 0.92) * mm});
            skLineSegment(sketch, "E378", {"start": v(-12.57, 0.92) * mm, "end": v(-12.66, 1.01) * mm});
            skLineSegment(sketch, "E379", {"start": v(-12.66, 1.01) * mm, "end": v(-12.7, 1.01) * mm});
            skLineSegment(sketch, "E380", {"start": v(-11.17, -1.4) * mm, "end": v(-11.17, -1.43) * mm});
            skLineSegment(sketch, "E381", {"start": v(-11.17, -1.43) * mm, "end": v(-11.27, -1.53) * mm});
            skLineSegment(sketch, "E382", {"start": v(-11.27, -1.53) * mm, "end": v(-11.3, -1.53) * mm});
            skLineSegment(sketch, "E383", {"start": v(-11.3, -1.53) * mm, "end": v(-11.68, -1.53) * mm});
            skLineSegment(sketch, "E384", {"start": v(-11.68, -1.53) * mm, "end": v(-11.7, -1.53) * mm});
            skLineSegment(sketch, "E385", {"start": v(-11.7, -1.53) * mm, "end": v(-11.8, -1.43) * mm});
            skLineSegment(sketch, "E386", {"start": v(-11.8, -1.43) * mm, "end": v(-11.8, -1.4) * mm});
            skLineSegment(sketch, "E387", {"start": v(-11.8, -1.4) * mm, "end": v(-11.8, 0.89) * mm});
            skLineSegment(sketch, "E388", {"start": v(-11.8, 0.89) * mm, "end": v(-11.8, 0.92) * mm});
            skLineSegment(sketch, "E389", {"start": v(-11.8, 0.92) * mm, "end": v(-11.7, 1.01) * mm});
            skLineSegment(sketch, "E390", {"start": v(-11.7, 1.01) * mm, "end": v(-11.68, 1.01) * mm});
            skLineSegment(sketch, "E391", {"start": v(-11.68, 1.01) * mm, "end": v(-11.3, 1.01) * mm});
            skLineSegment(sketch, "E392", {"start": v(-11.3, 1.01) * mm, "end": v(-11.27, 1.01) * mm});
            skLineSegment(sketch, "E393", {"start": v(-11.27, 1.01) * mm, "end": v(-11.17, 0.92) * mm});
            skLineSegment(sketch, "E394", {"start": v(-11.17, 0.92) * mm, "end": v(-11.17, 0.89) * mm});
            skLineSegment(sketch, "E395", {"start": v(-11.17, 0.89) * mm, "end": v(-11.17, -1.4) * mm});
            skLineSegment(sketch, "E396", {"start": v(3.52, 0.13) * mm, "end": v(4.02, 0.13) * mm});
            skLineSegment(sketch, "E397", {"start": v(4.02, 0.13) * mm, "end": v(4.05, 0.13) * mm});
            skLineSegment(sketch, "E398", {"start": v(4.05, 0.13) * mm, "end": v(4.15, 0.03) * mm});
            skLineSegment(sketch, "E399", {"start": v(4.15, 0.03) * mm, "end": v(4.15, 0) * mm});
            skLineSegment(sketch, "E400", {"start": v(4.15, 0) * mm, "end": v(4.15, -0.5) * mm});
            skLineSegment(sketch, "E401", {"start": v(4.15, -0.5) * mm, "end": v(4.15, -0.54) * mm});
            skLineSegment(sketch, "E402", {"start": v(4.15, -0.54) * mm, "end": v(4.05, -0.63) * mm});
            skLineSegment(sketch, "E403", {"start": v(4.05, -0.63) * mm, "end": v(4.02, -0.63) * mm});
            skLineSegment(sketch, "E404", {"start": v(4.02, -0.63) * mm, "end": v(3.52, -0.63) * mm});
            skLineSegment(sketch, "E405", {"start": v(3.52, -0.63) * mm, "end": v(3.5, -0.63) * mm});
            skLineSegment(sketch, "E406", {"start": v(3.5, -0.63) * mm, "end": v(3.4, -0.54) * mm});
            skLineSegment(sketch, "E407", {"start": v(3.4, -0.54) * mm, "end": v(3.4, -0.5) * mm});
            skLineSegment(sketch, "E408", {"start": v(3.4, -0.5) * mm, "end": v(3.4, 0) * mm});
            skLineSegment(sketch, "E409", {"start": v(3.4, 0) * mm, "end": v(3.4, 0.03) * mm});
            skLineSegment(sketch, "E410", {"start": v(3.4, 0.03) * mm, "end": v(3.5, 0.13) * mm});
            skLineSegment(sketch, "E411", {"start": v(3.5, 0.13) * mm, "end": v(3.52, 0.13) * mm});
            skSolve(sketch);
        }
        {
            var Q0;
            Q0=qSketchRegion(id+"F0",true);
            extrude(context, id + "F1", {"entities" : qUnion([Q0]), "depth" : 1.27 * mm});
        }
        {
            var Q0;
            Q0=qCreatedBy(makeId("Front.planeOp"),FACE);
            var sketch = newSketch(context, id + "F2", { "sketchPlane" : qUnion([Q0])});
            skLineSegment(sketch, "E412.bottom", {"start": v(-15.7, 0) * mm, "end": v(15.67, 0) * mm});
            skLineSegment(sketch, "E412.top", {"start": v(-15.7, -0.5) * mm, "end": v(15.67, -0.5) * mm});
            skLineSegment(sketch, "E412.left", {"start": v(-15.7, 0) * mm, "end": v(-15.7, -0.5) * mm});
            skLineSegment(sketch, "E412.right", {"start": v(15.67, 0) * mm, "end": v(15.67, -0.5) * mm});
            skSolve(sketch);
        }
        {
            var Q0;
            Q0 = qSketchRegion(id + "F2", true);
            extrude(context, id + "F3", {"entities" : qUnion([Q0]), "depth" : 0.5 * mm});
        }
    });
